# Revit family: P-Trap-American_Standard-Decorative-7720.018_Series
name_source: partatom
category: Pipe Fittings
revit_build: Autodesk Revit 2015 (Build: 20140606_1530(x64)
units: mm (PartAtom-declared; Revit-internal decimal feet)

## types (2) — shared parameters
Assembly Code = D2030100
CW Connection = No
Default Elevation = 20"
Description = Decorative P-Trap
HW Connection = No
Height = 7 1/8"
Installation Type = Wall Mounted
Length = 9 3/4"
Manufacturer = American Standard
Price = Prices may vary. Please consult Manufacturer Representative for most up-to-date price list.
Product Page URL = https://www.americanstandard-us.com
Sanitary Diameter = 1 1/4"
Sanitary Radius = 5/8"
URL = https://www.americanstandard-us.com
Vent Connection = No
Warranty Information = Lifetime Limited Warranty
Waste Connection = Yes
Width = 2 1/8"

## per-type parameters (varying)
| type | Material |
| 7720.018.002 | Brass-American Standard-002-Chrome |
| 7720.018.295 | Brass-American Standard-295-Brushed Nickel |

note: column(s) folded — value = type name in every type: Model

## geometry (parser evidence)
native form markers: Sweep x3
no freeform markers — native parametric forms only
